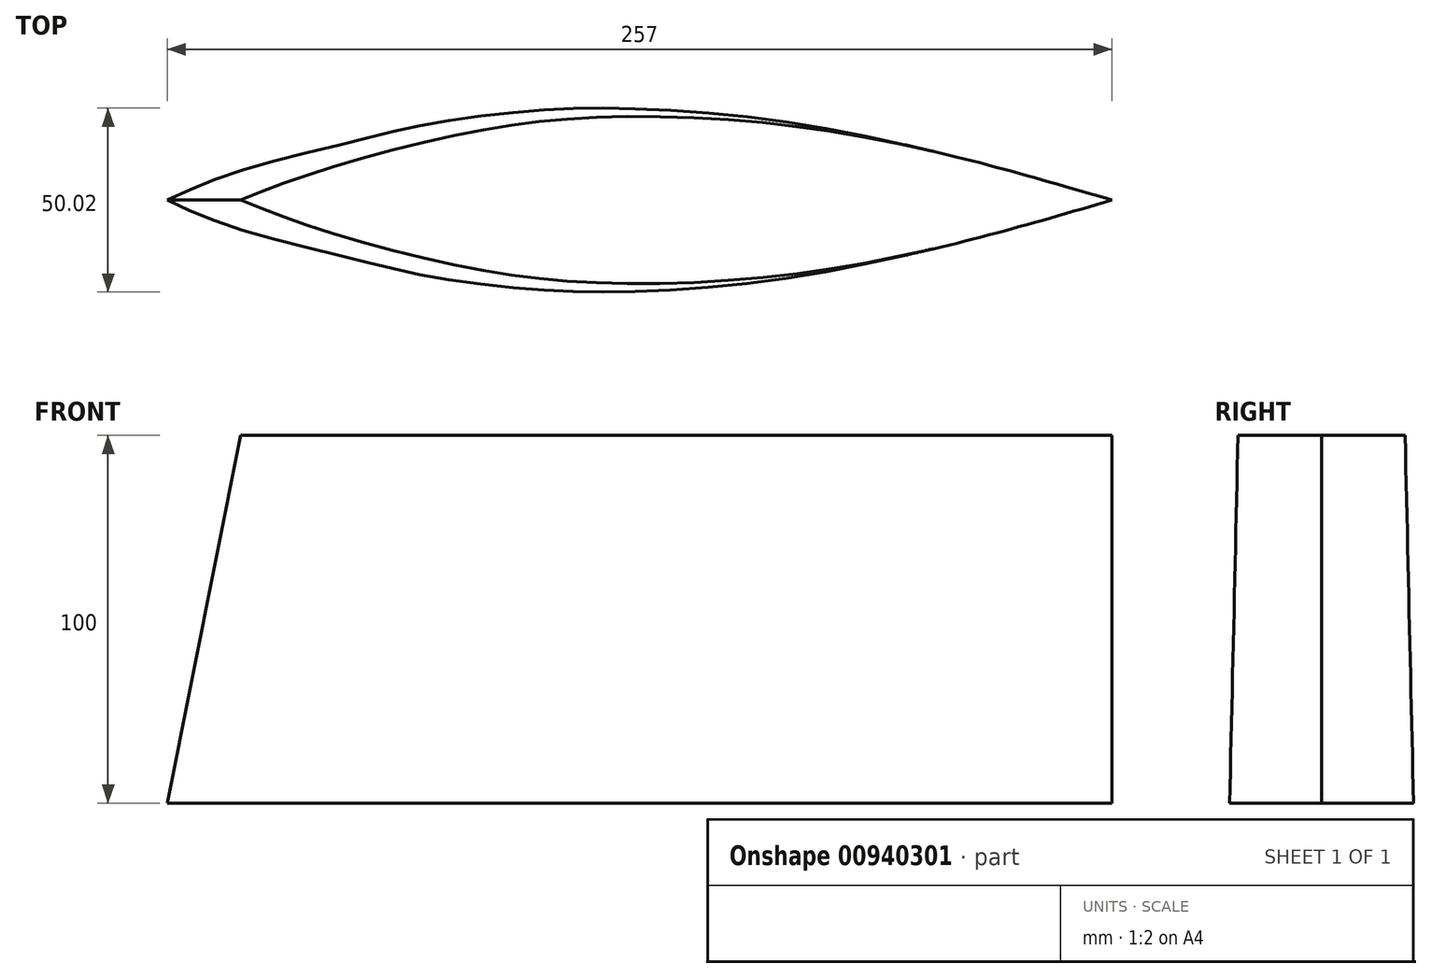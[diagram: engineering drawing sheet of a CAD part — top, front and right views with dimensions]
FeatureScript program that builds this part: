
annotation { "Feature Type Name" : "Feature", "Feature Type Description" : "" }
export const myFeature = defineFeature(function(context is Context, id is Id, definition is map)
    precondition{}
    {
        {
            var Q0;
            Q0=qCreatedBy(makeId("Top.planeOp"),FACE);
            var sketch = newSketch(context, id + "F0", { "sketchPlane" : qUnion([Q0])});
            skLineSegment(sketch, "E0", {"start": v(-257, 0) * mm, "end": v(0, 0) * mm});
            skFitSpline(sketch, "E1", {"points": [v(-257, 0) * mm, v(-238.01, -7.75) * mm, v(-207.74, -15.6) * mm, v(-187.18, -20.46) * mm, v(-158.78, -24.2) * mm, v(-133, -24.94) * mm, v(-93.38, -21.95) * mm, v(-47.79, -12.98) * mm, v(0, 0) * mm], "startDerivative": vector(172.72, -80.03) * mm, "endDerivative": vector(308.9, 87.74) * mm});
            skSolve(sketch);
        }
        {
            var Q0;
            Q0=qCreatedBy(makeId("Top.planeOp"),FACE);
            cPlane(context, id + "F1", {"entities" : qUnion([Q0]), "cplaneType" : CPlaneType.OFFSET, "offset" : 100 * mm, "width" : 150 * mm, "height" : 150 * mm});
        }
        {
            var Q0;
            Q0=qCreatedBy(id+"F1.planeOp",FACE);
            var sketch = newSketch(context, id + "F2", { "sketchPlane" : qUnion([Q0])});
            skLineSegment(sketch, "E2", {"start": v(-237, 0) * mm, "end": v(0, 0) * mm});
            skFitSpline(sketch, "E3", {"points": [v(-237, 0) * mm, v(-214.02, -8.43) * mm, v(-175.35, -18.3) * mm, v(-142.02, -22.42) * mm, v(-96.35, -21.19) * mm, v(-47.39, -12.96) * mm, v(0, 0) * mm], "startDerivative": vector(161.08, -64.14) * mm, "endDerivative": vector(254.58, 74.75) * mm});
            skSolve(sketch);
        }
        {
            var Q0;
            Q0=makeQuery(id+"F2.imprint","IMPRINT",FACE,{"disambiguationData":[TD([[makeQuery(id+"F2.imprint","IMPRINT",EDGE,{"derivedFrom":sQuery(id+"F2.wireOp",EDGE,"E2")}),-1.0]])]});
            var Q1;
            Q1=makeQuery(id+"F0.imprint","IMPRINT",FACE,{"disambiguationData":[TD([[makeQuery(id+"F0.imprint","IMPRINT",EDGE,{"derivedFrom":sQuery(id+"F0.wireOp",EDGE,"E0")}),-1.0]])]});
            loft(context, id + "F3", {"sheetProfilesArray" : [{ "sheetProfileEntities" : qUnion([Q0]) }, { "sheetProfileEntities" : qUnion([Q1]) }]});
        }
        {
            var Q0;
            Q0=makeQuery(id+"F3.opLoft","SWEPT_BODY",BODY,{"disambiguationData":[OSD([makeQuery(id+"F0.imprint","IMPRINT",FACE,{"disambiguationData":[TD([[makeQuery(id+"F0.imprint","IMPRINT",EDGE,{"derivedFrom":sQuery(id+"F0.wireOp",EDGE,"E0")}),-1.0]])]}),makeQuery(id+"F2.imprint","IMPRINT",FACE,{"disambiguationData":[TD([[makeQuery(id+"F2.imprint","IMPRINT",EDGE,{"derivedFrom":sQuery(id+"F2.wireOp",EDGE,"E2")}),-1.0]])]})])]});
            var Q1;
            Q1=qCreatedBy(makeId("Front.planeOp"),FACE);
            mirror(context, id + "F4", {"operationType" : NewBodyOperationType.ADD, "entities" : qUnion([Q0]), "mirrorPlane" : qUnion([Q1])});
        }
    });
